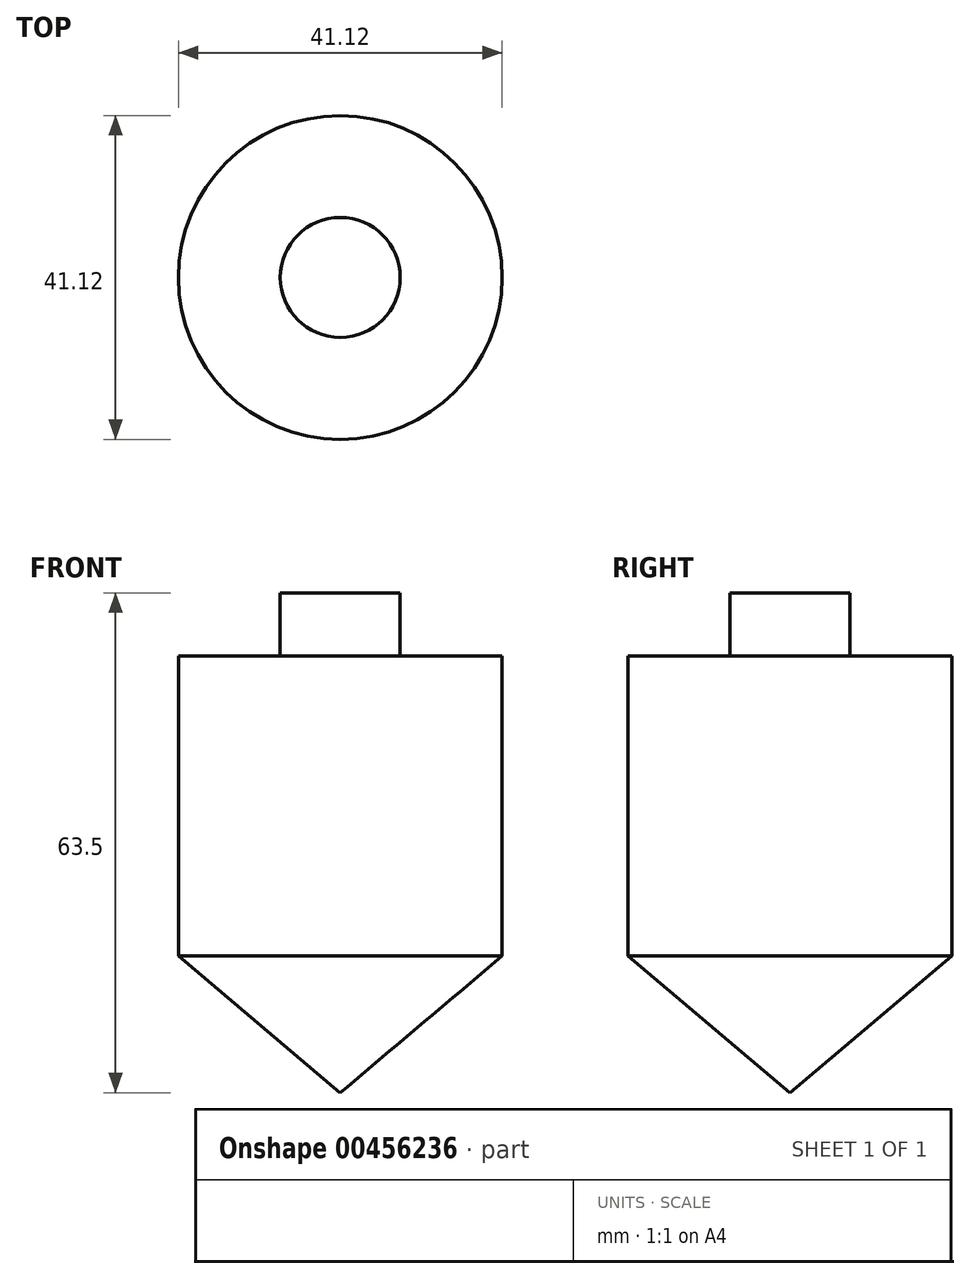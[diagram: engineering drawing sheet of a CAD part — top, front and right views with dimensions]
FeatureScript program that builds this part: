
annotation { "Feature Type Name" : "Feature", "Feature Type Description" : "" }
export const myFeature = defineFeature(function(context is Context, id is Id, definition is map)
    precondition{}
    {
        {
            var Q0;
            Q0=qCreatedBy(makeId("Front.planeOp"),FACE);
            var sketch = newSketch(context, id + "F0", { "sketchPlane" : qUnion([Q0])});
            skLineSegment(sketch, "E0", {"start": v(0, 0) * mm, "end": v(20.56, 17.35) * mm});
            skLineSegment(sketch, "E1", {"start": v(20.56, 17.35) * mm, "end": v(20.56, 55.45) * mm});
            skLineSegment(sketch, "E2", {"start": v(20.56, 55.45) * mm, "end": v(7.62, 55.45) * mm});
            skLineSegment(sketch, "E3", {"start": v(7.62, 55.45) * mm, "end": v(7.62, 63.5) * mm});
            skLineSegment(sketch, "E4", {"start": v(7.62, 63.5) * mm, "end": v(0, 63.5) * mm});
            skLineSegment(sketch, "E5", {"start": v(0, 63.5) * mm, "end": v(0, 0) * mm});
            skSolve(sketch);
        }
        {
            var Q0;
            Q0=makeQuery(id+"F0.imprint","IMPRINT",FACE,{"disambiguationData":[TD([[makeQuery(id+"F0.imprint","IMPRINT",EDGE,{"derivedFrom":sQuery(id+"F0.wireOp",EDGE,"E0")}),1.0]])]});
            var Q1;
            Q1=sQuery(id+"F0.wireOp",EDGE,"E5");
            revolve(context, id + "F1", {"entities" : qUnion([Q0]), "axis" : qUnion([Q1]), "revolveType" : RevolveType.FULL});
        }
    });
